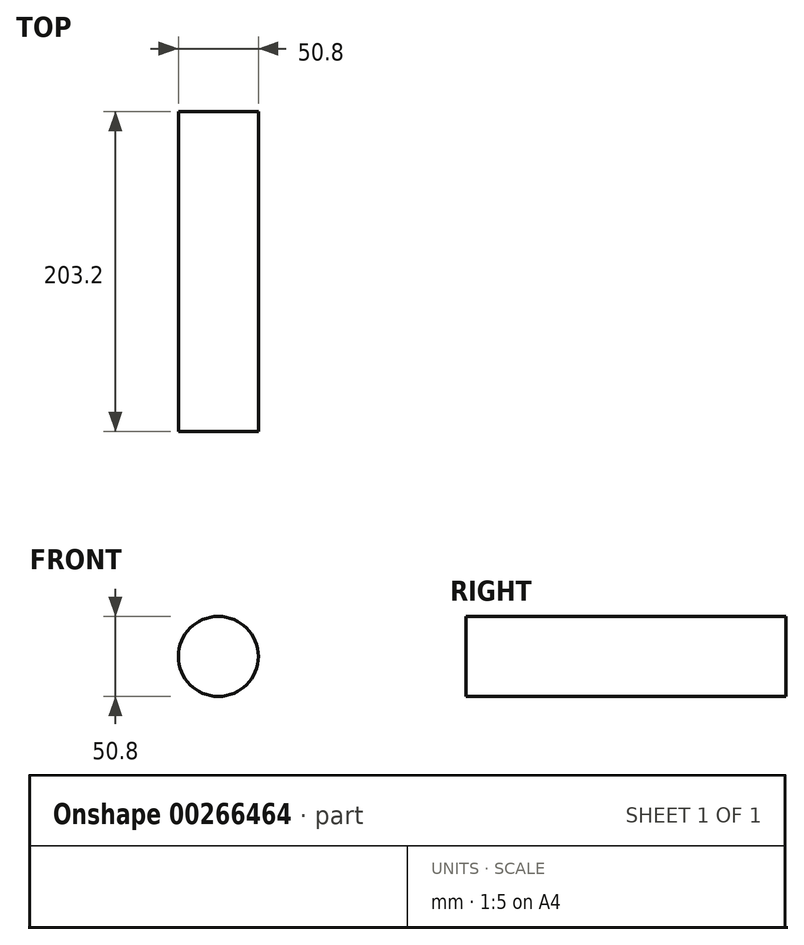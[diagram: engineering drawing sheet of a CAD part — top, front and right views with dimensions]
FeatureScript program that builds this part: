
annotation { "Feature Type Name" : "Feature", "Feature Type Description" : "" }
export const myFeature = defineFeature(function(context is Context, id is Id, definition is map)
    precondition{}
    {
        {
            var Q0;
            Q0=qCreatedBy(makeId("Front.planeOp"),FACE);
            var sketch = newSketch(context, id + "F0", { "sketchPlane" : qUnion([Q0])});
            skCircle(sketch, "E0", {"center": v(0, 0) * mm, "radius": 25.4 * mm});
            skSolve(sketch);
        }
        {
            var Q0;
            Q0 = qSketchRegion(id + "F0", true);
            extrude(context, id + "F1", {"entities" : qUnion([Q0]), "depth" : 203.2 * mm});
        }
    });
